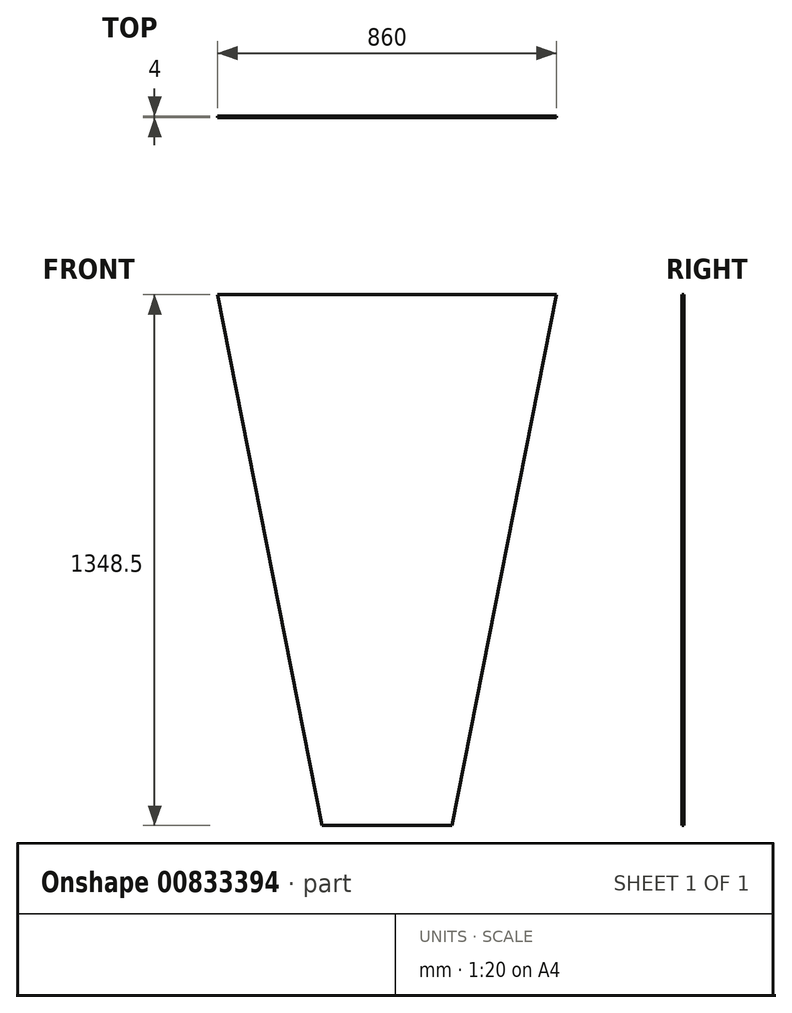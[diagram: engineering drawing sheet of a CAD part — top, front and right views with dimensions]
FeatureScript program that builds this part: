
annotation { "Feature Type Name" : "Feature", "Feature Type Description" : "" }
export const myFeature = defineFeature(function(context is Context, id is Id, definition is map)
    precondition{}
    {
        {
            var Q0;
            Q0=qCreatedBy(makeId("Front.planeOp"),FACE);
            var sketch = newSketch(context, id + "F0", { "sketchPlane" : qUnion([Q0])});
            skLineSegment(sketch, "E0", {"start": v(0, 0) * mm, "end": v(0, 1348.5) * mm, "construction": true});
            skLineSegment(sketch, "E1", {"start": v(0, 1348.5) * mm, "end": v(430, 1348.5) * mm});
            skLineSegment(sketch, "E2", {"start": v(430, 1348.5) * mm, "end": v(165, 0) * mm});
            skLineSegment(sketch, "E3", {"start": v(165, 0) * mm, "end": v(0, 0) * mm});
            skLineSegment(sketch, "E4.MirrorCS", {"start": v(0, 1348.5) * mm, "end": v(-430, 1348.5) * mm});
            skLineSegment(sketch, "E5.MirrorCS", {"start": v(-430, 1348.5) * mm, "end": v(-165, 0) * mm});
            skLineSegment(sketch, "E6.MirrorCS", {"start": v(-165, 0) * mm, "end": v(0, 0) * mm});
            skSolve(sketch);
        }
        {
            var Q0;
            Q0 = qSketchRegion(id + "F0", true);
            extrude(context, id + "F1", {"entities" : qUnion([Q0]), "depth" : 4 * mm, "offsetDistance" : 25 * mm});
        }
    });
